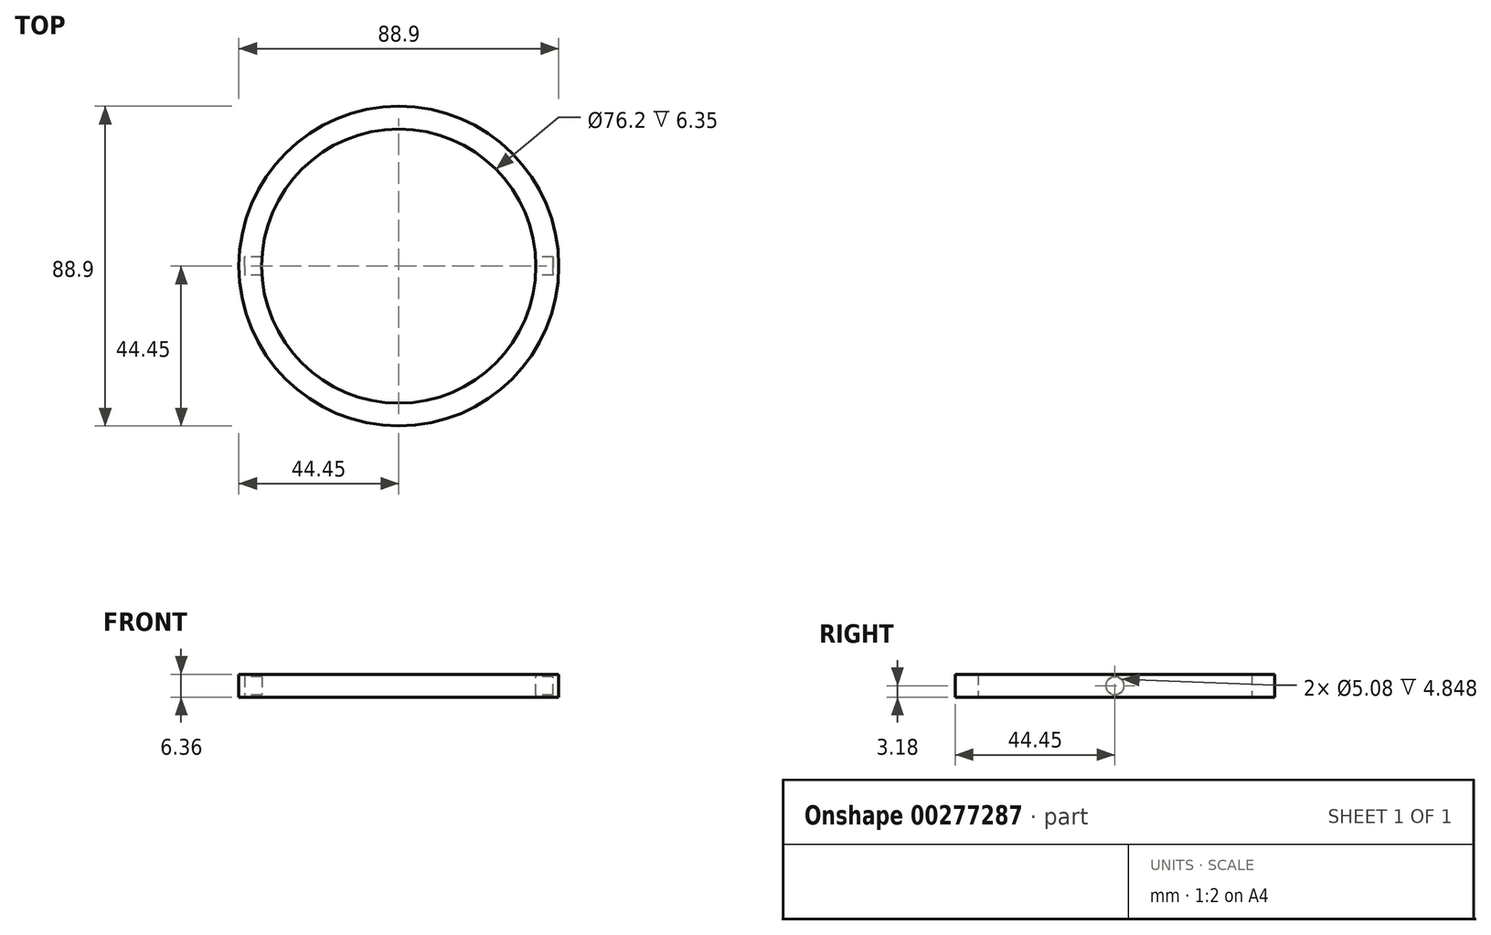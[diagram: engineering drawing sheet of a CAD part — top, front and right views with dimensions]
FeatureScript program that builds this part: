
annotation { "Feature Type Name" : "Feature", "Feature Type Description" : "" }
export const myFeature = defineFeature(function(context is Context, id is Id, definition is map)
    precondition{}
    {
        {
            var Q0;
            Q0=qCreatedBy(makeId("Top.planeOp"),FACE);
            var sketch = newSketch(context, id + "F0", { "sketchPlane" : qUnion([Q0])});
            skCircle(sketch, "E0", {"center": v(0, 0) * mm, "radius": 44.45 * mm});
            skCircle(sketch, "E1.0", {"center": v(0, 0) * mm, "radius": 38.1 * mm});
            skSolve(sketch);
        }
        {
            var Q0;
            Q0=makeQuery(id+"F0.imprint","IMPRINT",FACE,{"disambiguationData":[TD([[makeQuery(id+"F0.imprint","IMPRINT",EDGE,{"derivedFrom":sQuery(id+"F0.wireOp",EDGE,"E0")}),1.0]])]});
            extrude(context, id + "F1", {"entities" : qUnion([Q0]), "endBound" : BoundingType.SYMMETRIC, "depth" : 6.35 * mm});
        }
        {
            var Q0;
            Q0=qCreatedBy(makeId("Right.planeOp"),FACE);
            var sketch = newSketch(context, id + "F2", { "sketchPlane" : qUnion([Q0])});
            skCircle(sketch, "E2", {"center": v(0, 0) * mm, "radius": 2.54 * mm});
            skSolve(sketch);
        }
        {
            var Q0;
            Q0 = qSketchRegion(id + "F2", true);
            extrude(context, id + "F3", {"entities" : qUnion([Q0]), "operationType" : NewBodyOperationType.REMOVE, "endBound" : BoundingType.SYMMETRIC, "depth" : 85.72 * mm});
        }
    });
